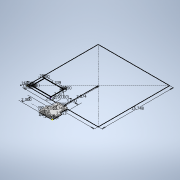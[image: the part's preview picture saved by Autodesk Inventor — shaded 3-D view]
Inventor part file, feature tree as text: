
AUTODESK INVENTOR PART (.ipt)
format: ipt  version: 2020 (Build 240168000, 168)  size: 285,184 bytes
history: native  units: in
note: dims shown in document units (in); Inventor stores cm internally (conversion verified against a paired STEP export)
features: sketch x6, extrude x6, hole x3, pattern_linear x1
ambient origin geometry x8: Origin, YZ Plane, XZ Plane, XY Plane, X Axis, Y Axis, Z Axis, Center Point
bodies: Solid1 (feature_tree)
feature tree (16):
  sketch  "Sketch1"  dims[d0=3.0in d1=2.0in]
  extrude  "Extrusion1"  Depth=2.0in
  hole  "Hole1"  [1 undecoded]
  sketch  "Sketch2"  dims[d2=0.25in d3=1.0in]
  extrude  "Extrusion2"  TaperAngle=0.0deg  [1 undecoded]
  hole  "Hole2"  [1 undecoded]
  extrude  "Extrusion3"  Depth=0.25in
  pattern_linear  "Rectangular Pattern1"  Spacing1=90.0deg  [1 undecoded]
  extrude  "Extrusion4"  Depth=0.125in
  extrude  "Extrusion5"  Depth=0.125in
  hole  "Hole3"  [1 undecoded]
  extrude  "Extrusion6"  TaperAngle=90.0deg  [1 undecoded]
  sketch  "Sketch3"  dims[d4=1.0in d5=0.0in]
  sketch  "Sketch4"  dims[d6=0.5in d7=0.5in]
  sketch  "Sketch5"  dims[d8=0.25in d9=0.25in]
  sketch  "Sketch6"  dims[d10=2.9528in d11=90.0deg d12=2.9528in d13=1.0in d14=7.874in d15=90.0deg d16=15.748in d17=15.748in d18=0.25in d19=0.0in d20=0.26in d21=0.5in d22=0.375in d23=0.25in d24=0.5635in d25=1.0in d26=0.8108in d27=0.25in d28=90.0deg d29=0.25in d30=0.25in d31=0.25in d32=4.3386in d33=2.9134in d34=0.25in d35=0.25in d36=0.25in d37=0.25in d38=0.25in d39=0.315in d40=90.0deg d41=0.0787in d42=0.0787in d43=0.0787in d44=0.0787in d45=0.0in d46=0.0in d47=0.203in d48=0.625in d49=0.375in d50=0.25in d51=0.5635in d52=1.0in d53=0.8108in d54=0.0787in d55=0.0in d56=1.1811in d58=4.839in d59=1.5748in d61=3.423in d62=0.25in d63=0.25in d64=0.0in d65=0.0in d66=1.0in d67=0.0in d68=0.25in d69=0.5in d70=90.0deg d71=1.0in d72=0.266in d73=0.75in d74=0.438in d75=0.25in d76=0.5635in d77=1.0in d78=0.8108in d79=1.5in d80=0.125in d81=0.125in d82=0.0in]
note: 6 required parameter values undecoded (feature->parameter linkage not recoverable at this tier; creation-order binding heuristic only, values carry confidence <= 0.55)
